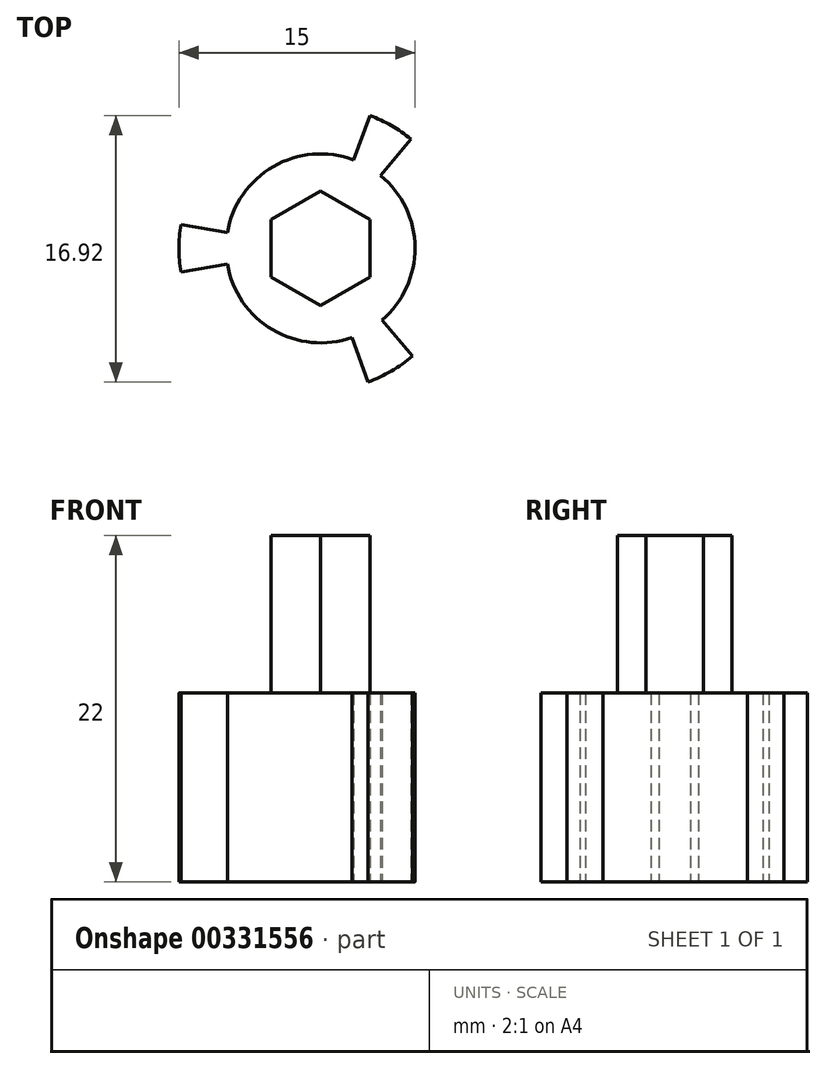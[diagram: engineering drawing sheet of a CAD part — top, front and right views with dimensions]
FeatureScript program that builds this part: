
annotation { "Feature Type Name" : "Feature", "Feature Type Description" : "" }
export const myFeature = defineFeature(function(context is Context, id is Id, definition is map)
    precondition{}
    {
        {
            var Q0;
            Q0=qCreatedBy(makeId("Top.planeOp"),FACE);
            var sketch = newSketch(context, id + "F0", { "sketchPlane" : qUnion([Q0])});
            skCircle(sketch, "E0", {"center": v(0, 0) * mm, "radius": 9 * mm});
            skCircle(sketch, "E1.cCircle", {"center": v(0, 0) * mm, "radius": 9 * mm, "construction": true});
            skLineSegment(sketch, "E1.0", {"start": v(-9, 0) * mm, "end": v(4.5, 7.8) * mm, "construction": true});
            skLineSegment(sketch, "E1.1", {"start": v(4.5, 7.8) * mm, "end": v(4.5, -7.8) * mm, "construction": true});
            skLineSegment(sketch, "E1.2", {"start": v(4.5, -7.8) * mm, "end": v(-9, 0) * mm, "construction": true});
            skCircle(sketch, "E2", {"center": v(0, 0) * mm, "radius": 6 * mm});
            skPoint(sketch, "E3", {"position": v(-8.87, 1.5) * mm});
            skPoint(sketch, "E4", {"position": v(-8.87, -1.5) * mm});
            skLineSegment(sketch, "E5", {"start": v(-8.87, 1.5) * mm, "end": v(-5.92, 1) * mm});
            skLineSegment(sketch, "E6", {"start": v(-8.87, -1.5) * mm, "end": v(-5.92, -1) * mm});
            skPoint(sketch, "E7", {"position": v(3.14, 8.43) * mm});
            skPoint(sketch, "E8", {"position": v(5.73, 6.94) * mm});
            skPoint(sketch, "E9", {"position": v(5.85, -6.84) * mm});
            skPoint(sketch, "E10", {"position": v(3, -8.49) * mm});
            skLineSegment(sketch, "E11", {"start": v(4.5, 7.8) * mm, "end": v(0, 0) * mm, "construction": true});
            skLineSegment(sketch, "E12", {"start": v(4.5, -7.8) * mm, "end": v(0, 0) * mm, "construction": true});
            skLineSegment(sketch, "E13", {"start": v(3.14, 8.43) * mm, "end": v(2.1, 5.62) * mm});
            skLineSegment(sketch, "E14", {"start": v(5.73, 6.94) * mm, "end": v(3.82, 4.63) * mm});
            skLineSegment(sketch, "E15", {"start": v(5.85, -6.84) * mm, "end": v(3.9, -4.56) * mm});
            skLineSegment(sketch, "E16", {"start": v(3, -8.49) * mm, "end": v(2, -5.66) * mm});
            skSolve(sketch);
        }
        {
            var Q0;
            {var subQ0=sQuery(id+"F0.wireOp",EDGE,"E5");Q0=makeQuery(id+"F0.imprint","IMPRINT",FACE,{"disambiguationData":[TD([[makeQuery(id+"F0.imprint","IMPRINT",EDGE,{"derivedFrom":subQ0}),-1.0]])]});}
            var Q1;
            {var subQ0=sQuery(id+"F0.wireOp",EDGE,"E2");var subQ4=makeQuery(id+"F0.imprint","INTERSECT",VERTEX,{"derivedFrom":[subQ0,sQuery(id+"F0.wireOp",EDGE,"E13")]});Q1=makeQuery(id+"F0.imprint","IMPRINT",FACE,{"disambiguationData":[TD([[makeQuery(id+"F0.imprint","IMPRINT",EDGE,{"disambiguationData":[TD([[subQ4,1.0]])],"derivedFrom":subQ0}),1.0]])]});}
            var Q2;
            {var subQ0=sQuery(id+"F0.wireOp",EDGE,"E13");Q2=makeQuery(id+"F0.imprint","IMPRINT",FACE,{"disambiguationData":[TD([[makeQuery(id+"F0.imprint","IMPRINT",EDGE,{"derivedFrom":subQ0}),1.0]])]});}
            var Q3;
            {var subQ0=sQuery(id+"F0.wireOp",EDGE,"E15");Q3=makeQuery(id+"F0.imprint","IMPRINT",FACE,{"disambiguationData":[TD([[makeQuery(id+"F0.imprint","IMPRINT",EDGE,{"derivedFrom":subQ0}),1.0]])]});}
            extrude(context, id + "F1", {"entities" : qUnion([Q0, Q1, Q2, Q3]), "depth" : 12 * mm});
        }
        {
            var Q0;
            Q0=makeQuery(id+"F1.opExtrude","CAP_FACE",FACE,{"disambiguationData":[OSD([sQuery(id+"F0.wireOp",EDGE,"E0"),sQuery(id+"F0.wireOp",EDGE,"E2"),sQuery(id+"F0.wireOp",EDGE,"E5"),sQuery(id+"F0.wireOp",EDGE,"E6"),sQuery(id+"F0.wireOp",EDGE,"E13"),sQuery(id+"F0.wireOp",EDGE,"E14"),sQuery(id+"F0.wireOp",EDGE,"E15"),sQuery(id+"F0.wireOp",EDGE,"E16")])],"isStart":false});
            var sketch = newSketch(context, id + "F2", { "sketchPlane" : qUnion([Q0])});
            skCircle(sketch, "E17", {"center": v(0, 0) * mm, "radius": 3.15 * mm});
            skCircle(sketch, "E18.cCircle", {"center": v(0, 0) * mm, "radius": 3.15 * mm, "construction": true});
            skLineSegment(sketch, "E18.0", {"start": v(-3.15, -1.82) * mm, "end": v(-3.15, 1.82) * mm});
            skLineSegment(sketch, "E18.1", {"start": v(-3.15, 1.82) * mm, "end": v(0, 3.64) * mm});
            skLineSegment(sketch, "E18.2", {"start": v(0, 3.64) * mm, "end": v(3.15, 1.82) * mm});
            skLineSegment(sketch, "E18.3", {"start": v(3.15, 1.82) * mm, "end": v(3.15, -1.82) * mm});
            skLineSegment(sketch, "E18.4", {"start": v(3.15, -1.82) * mm, "end": v(0, -3.64) * mm});
            skLineSegment(sketch, "E18.5", {"start": v(0, -3.64) * mm, "end": v(-3.15, -1.82) * mm});
            skPoint(sketch, "E18.0.midPoint", {"position": v(-3.15, 0) * mm});
            skSolve(sketch);
        }
        {
            var Q0;
            Q0=qSketchRegion(id+"F2",true);
            extrude(context, id + "F3", {"entities" : qUnion([Q0]), "operationType" : NewBodyOperationType.ADD, "depth" : 10 * mm});
        }
    });
